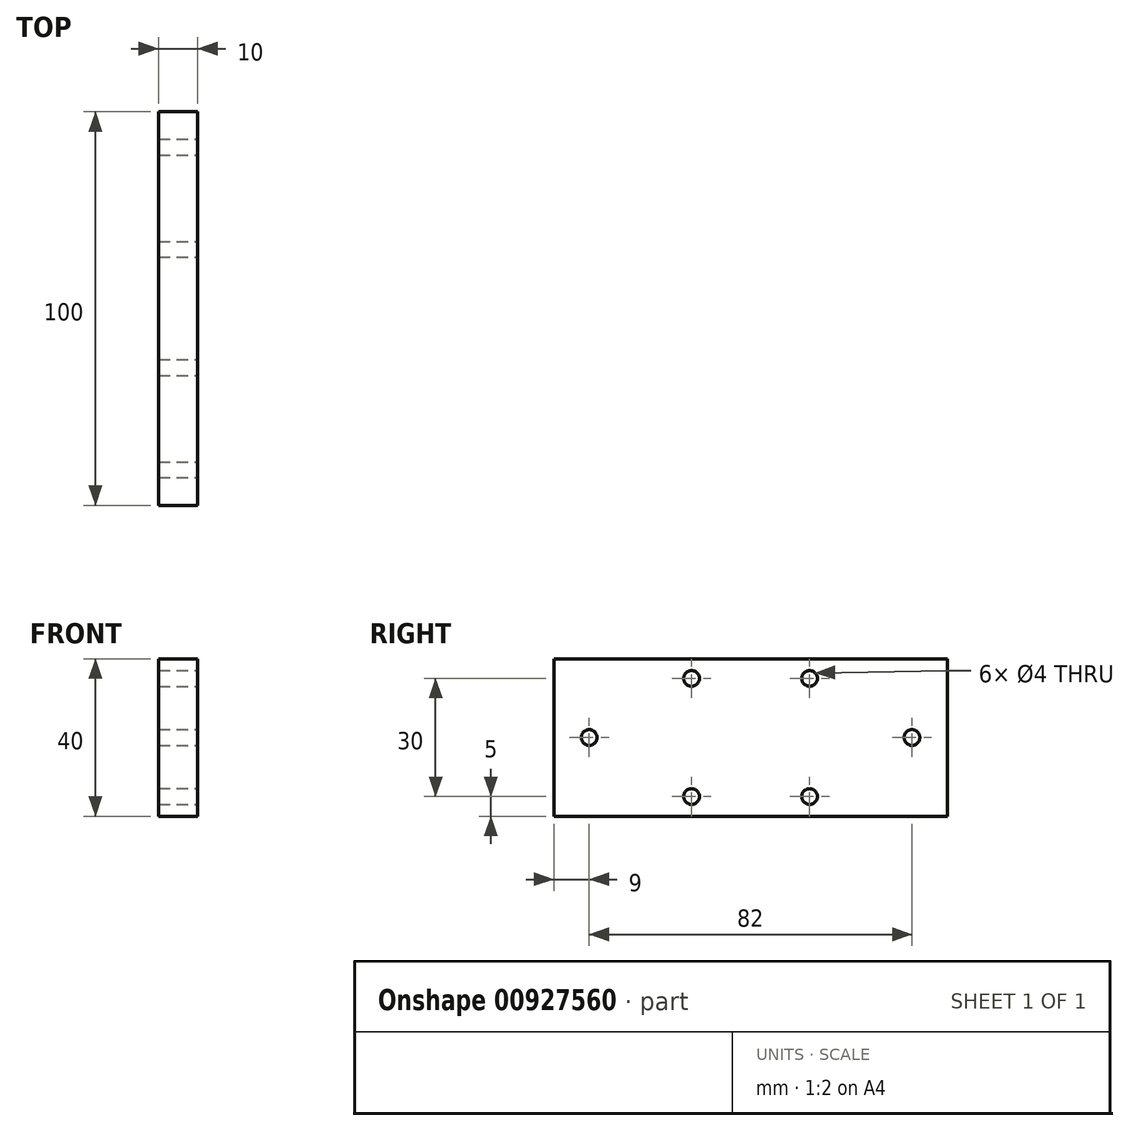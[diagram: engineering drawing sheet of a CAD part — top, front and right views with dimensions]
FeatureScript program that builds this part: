
annotation { "Feature Type Name" : "Feature", "Feature Type Description" : "" }
export const myFeature = defineFeature(function(context is Context, id is Id, definition is map)
    precondition{}
    {
        {
            var Q0;
            Q0=qCreatedBy(makeId("Right.planeOp"),FACE);
            var sketch = newSketch(context, id + "F0", { "sketchPlane" : qUnion([Q0])});
            skLineSegment(sketch, "E0.bottom", {"start": v(50, 20) * mm, "end": v(-50, 20) * mm});
            skLineSegment(sketch, "E0.top", {"start": v(50, -20) * mm, "end": v(-50, -20) * mm});
            skLineSegment(sketch, "E0.left", {"start": v(50, 20) * mm, "end": v(50, -20) * mm});
            skLineSegment(sketch, "E0.right", {"start": v(-50, 20) * mm, "end": v(-50, -20) * mm});
            skPoint(sketch, "E0.middle", {"position": v(0, 0) * mm});
            skSolve(sketch);
        }
        {
            var Q0;
            Q0 = qSketchRegion(id + "F0", true);
            extrude(context, id + "F1", {"entities" : qUnion([Q0]), "depth" : 10 * mm, "offsetDistance" : 25 * mm});
        }
        {
            var Q0;
            Q0=makeQuery(id+"F1.opExtrude","CAP_FACE",FACE,{"disambiguationData":[OSD([sQuery(id+"F0.wireOp",EDGE,"E0.bottom"),sQuery(id+"F0.wireOp",EDGE,"E0.top"),sQuery(id+"F0.wireOp",EDGE,"E0.left"),sQuery(id+"F0.wireOp",EDGE,"E0.right")])],"isStart":false});
            var sketch = newSketch(context, id + "F2", { "sketchPlane" : qUnion([Q0])});
            skLineSegment(sketch, "E1", {"start": v(-45.86, 15) * mm, "end": v(55.3, 15) * mm, "construction": true});
            skLineSegment(sketch, "E2", {"start": v(-41.24, -15) * mm, "end": v(54.45, -15) * mm, "construction": true});
            skLineSegment(sketch, "E3", {"start": v(15, 39.61) * mm, "end": v(15, -40.55) * mm, "construction": true});
            skLineSegment(sketch, "E4.MirrorCS", {"start": v(-15, 39.61) * mm, "end": v(-15, -40.55) * mm, "construction": true});
            skCircle(sketch, "E5", {"center": v(-15, 15) * mm, "radius": 2 * mm});
            skCircle(sketch, "E6", {"center": v(15, 15) * mm, "radius": 2 * mm});
            skCircle(sketch, "E7", {"center": v(-15, -15) * mm, "radius": 2 * mm});
            skCircle(sketch, "E8", {"center": v(15, -15) * mm, "radius": 2 * mm});
            skSolve(sketch);
        }
        {
            var Q0;
            Q0=makeQuery(id+"F2.imprint","IMPRINT",FACE,{"disambiguationData":[TD([[makeQuery(id+"F2.imprint","IMPRINT",EDGE,{"derivedFrom":sQuery(id+"F2.wireOp",EDGE,"E5")}),1.0]])]});
            var Q1;
            Q1=makeQuery(id+"F2.imprint","IMPRINT",FACE,{"disambiguationData":[TD([[makeQuery(id+"F2.imprint","IMPRINT",EDGE,{"derivedFrom":sQuery(id+"F2.wireOp",EDGE,"E6")}),1.0]])]});
            var Q2;
            Q2=makeQuery(id+"F2.imprint","IMPRINT",FACE,{"disambiguationData":[TD([[makeQuery(id+"F2.imprint","IMPRINT",EDGE,{"derivedFrom":sQuery(id+"F2.wireOp",EDGE,"E7")}),1.0]])]});
            var Q3;
            Q3=makeQuery(id+"F2.imprint","IMPRINT",FACE,{"disambiguationData":[TD([[makeQuery(id+"F2.imprint","IMPRINT",EDGE,{"derivedFrom":sQuery(id+"F2.wireOp",EDGE,"E8")}),1.0]])]});
            extrude(context, id + "F3", {"entities" : qUnion([Q0, Q1, Q2, Q3]), "operationType" : NewBodyOperationType.REMOVE, "endBound" : BoundingType.THROUGH_ALL, "oppositeDirection" : true, "depth" : 25 * mm, "offsetDistance" : 25 * mm});
        }
        {
            var Q0;
            Q0=makeQuery(id+"F1.opExtrude","CAP_FACE",FACE,{"disambiguationData":[OSD([sQuery(id+"F0.wireOp",EDGE,"E0.bottom"),sQuery(id+"F0.wireOp",EDGE,"E0.top"),sQuery(id+"F0.wireOp",EDGE,"E0.left"),sQuery(id+"F0.wireOp",EDGE,"E0.right")])],"isStart":false});
            var sketch = newSketch(context, id + "F4", { "sketchPlane" : qUnion([Q0])});
            skLineSegment(sketch, "E9", {"start": v(-54.98, 0) * mm, "end": v(69.7, 0) * mm, "construction": true});
            skPoint(sketch, "E9.startSnap0", {"position": v(-50, 0) * mm});
            skCircle(sketch, "E10", {"center": v(-41, 0) * mm, "radius": 2 * mm});
            skCircle(sketch, "E11.MirrorC", {"center": v(41, 0) * mm, "radius": 2 * mm});
            skSolve(sketch);
        }
        {
            var Q0;
            Q0 = qSketchRegion(id + "F4", true);
            extrude(context, id + "F5", {"entities" : qUnion([Q0]), "operationType" : NewBodyOperationType.REMOVE, "endBound" : BoundingType.THROUGH_ALL, "oppositeDirection" : true, "depth" : 25 * mm, "offsetDistance" : 25 * mm});
        }
    });
